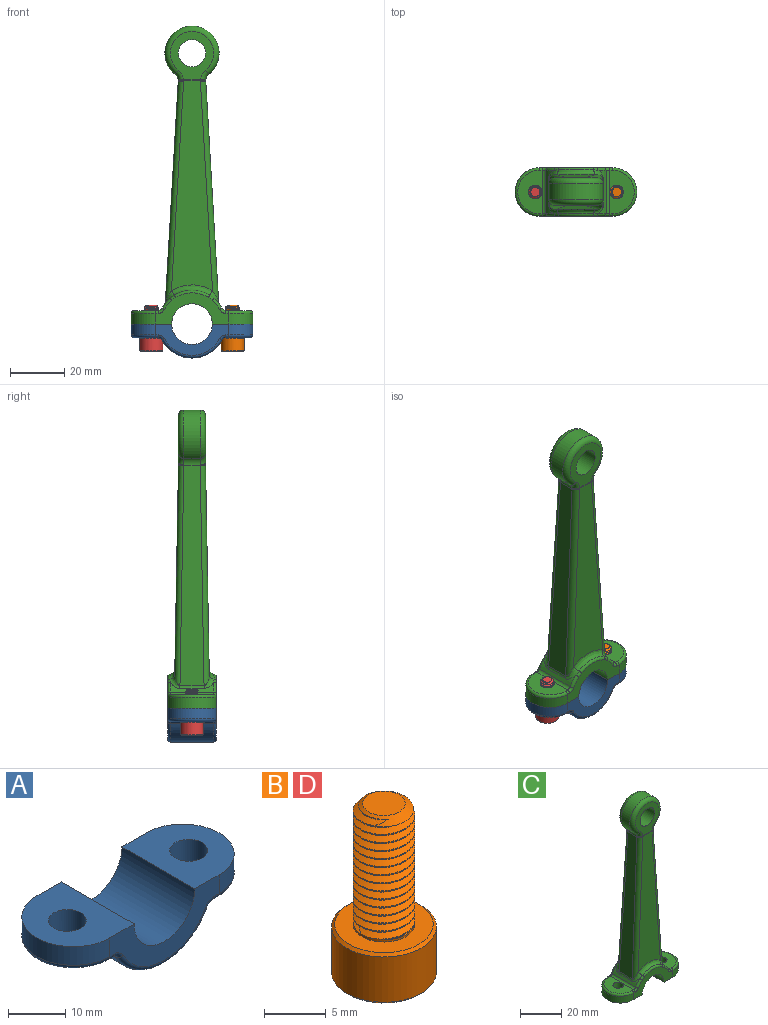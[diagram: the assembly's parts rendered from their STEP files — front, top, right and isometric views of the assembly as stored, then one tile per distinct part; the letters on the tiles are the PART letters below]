
ASSEMBLY  parts=4 mates=3
PART A: 30 faces, bbox 46.5x19.5x13.5 mm
  f0: cylinder r=12.5mm len=22.14mm, axis (0,1,0), area 404.5mm2, adj f12,f13,f14,f15,f16,f17,f23,f24
  f1: plane 18x15mm, normal (0,0,1), area 201mm2, adj f2,f6,f7,f9,f10
  f2: cylinder r=7.5mm len=18mm, axis (0,1,0), area 424.1mm2, adj f1,f3,f6,f7
  f3: plane 18x15mm, normal (0,0,1), area 201mm2, adj f2,f6,f7,f8,f11
  f4: plane 16x12mm, normal (0,0,-1), area 103.9mm2, adj f11,f12,f14,f17,f27,f28,f29
  f5: plane 16x12mm, normal (0,0,-1), area 103.9mm2, adj f10,f13,f15,f16,f18,f19,f20
  f6: plane 27x11.5mm, normal (0,-1,0), area 138.1mm2, adj f1,f2,f3,f8,f9,f19,f21,f23
  f7: plane 27x11.5mm, normal (0,1,0), area 138.1mm2, adj f1,f2,f3,f8,f9,f20,f22,f24
  f8: cylinder r=9mm len=18mm, axis (0,0,1), area 113.1mm2, adj f3,f6,f7,f29
  f9: cylinder r=9mm len=18mm, axis (0,0,-1), area 113.1mm2, adj f1,f6,f7,f18
  f10: cylinder r=3.3mm len=6.6mm, axis (0,0,1), area 103.7mm2, adj f1,f5
  f11: cylinder r=3.3mm len=6.6mm, axis (0,0,1), area 103.7mm2, adj f3,f4
  f12: cylinder r=5.5mm len=9.69mm, axis (0,0,1), area 21.4mm2, adj f0,f4,f14,f17
  f13: cylinder r=5.5mm len=9.69mm, axis (0,0,1), area 21.4mm2, adj f0,f5,f15,f16
  f14: cylinder r=1.5mm len=4.15mm, axis (0,1,0), area 6mm2, adj f0,f4,f12,f26
  f15: cylinder r=1.5mm len=4.15mm, axis (0,1,0), area 6mm2, adj f0,f5,f13,f22
  f16: cylinder r=1.5mm len=4.15mm, axis (0,1,0), area 6mm2, adj f0,f5,f13,f21
  f17: cylinder r=1.5mm len=4.15mm, axis (0,1,0), area 6mm2, adj f0,f4,f12,f25
  f18: torus R=8mm, axis (0,0,-1), area 42.6mm2, adj f5,f9,f19,f20
  f19: cylinder r=1mm len=1.1mm, axis (-1,0,0), area 1.7mm2, adj f5,f6,f18,f21
  f20: cylinder r=1mm len=1.1mm, axis (1,0,0), area 1.7mm2, adj f5,f7,f18,f22
  f21: torus R=2.5mm, axis (0,-1,0), area 3.2mm2, adj f6,f16,f19,f23
  f22: torus R=2.5mm, axis (0,-1,0), area 3.2mm2, adj f7,f15,f20,f24
  f23: torus R=11.5mm, axis (0,-1,0), area 41.5mm2, adj f0,f6,f21,f25
  f24: torus R=11.5mm, axis (0,-1,0), area 41.5mm2, adj f0,f7,f22,f26
  f25: torus R=2.5mm, axis (0,-1,0), area 3.2mm2, adj f6,f17,f23,f27
  f26: torus R=2.5mm, axis (0,-1,0), area 3.2mm2, adj f7,f14,f24,f28
  f27: cylinder r=1mm len=1.1mm, axis (-1,0,0), area 1.7mm2, adj f4,f6,f25,f29
  f28: cylinder r=1mm len=1.1mm, axis (1,0,0), area 1.7mm2, adj f4,f7,f26,f29
  f29: torus R=8mm, axis (0,0,-1), area 42.6mm2, adj f4,f8,f27,f28
PART B: 39 faces, bbox 9.4x9.4x18 mm
  f0: cone r=2.5mm half-angle=67.5deg, axis (0,0,-1), area 4.1mm2, adj f1,f18,f19,f38
  f1: cylinder r=1.98mm len=11.41mm, axis (0,0,-1), area 17.7mm2, adj f0,f2,f18,f38
  f2: cone r=1.73mm half-angle=55deg, axis (0,0,-1), area 7.9mm2, adj f1,f3,f4,f18,f38
  f3: plane 3.45x3.45mm, normal (0,0,1), area 9.4mm2, adj f2
  f4: cylinder r=2.5mm len=5mm, axis (0,0,1), area 1mm2, adj f2,f5,f18,f38
  f5: cylinder r=2.5mm len=5mm, axis (0,0,1), area 1.6mm2, adj f4,f6,f18,f38
  f6: cylinder r=2.5mm len=5mm, axis (0,0,1), area 1.6mm2, adj f5,f7,f18,f38
  f7: cylinder r=2.5mm len=5mm, axis (0,0,1), area 1.6mm2, adj f6,f8,f18,f38
  f8: cylinder r=2.5mm len=5mm, axis (0,0,1), area 1.6mm2, adj f7,f9,f18,f38
  f9: cylinder r=2.5mm len=5mm, axis (0,0,1), area 1.6mm2, adj f8,f10,f18,f38
  f10: cylinder r=2.5mm len=5mm, axis (0,0,1), area 1.6mm2, adj f9,f11,f18,f38
  f11: cylinder r=2.5mm len=5mm, axis (0,0,1), area 1.6mm2, adj f10,f12,f18,f38
  f12: cylinder r=2.5mm len=5mm, axis (0,0,1), area 1.6mm2, adj f11,f13,f18,f38
  f13: cylinder r=2.5mm len=5mm, axis (0,0,1), area 1.6mm2, adj f12,f14,f18,f38
  f14: cylinder r=2.5mm len=5mm, axis (0,0,1), area 1.6mm2, adj f13,f15,f18,f38
  f15: cylinder r=2.5mm len=5mm, axis (0,0,1), area 1.6mm2, adj f14,f16,f18,f38
  f16: cylinder r=2.5mm len=5mm, axis (0,0,1), area 1.6mm2, adj f15,f17,f18,f38
  f17: cylinder r=2.5mm len=5mm, axis (0,0,1), area 1.6mm2, adj f16,f18,f19,f38
  f18: bspline ~11.71x5mm, area 119.7mm2, adj f0,f1,f2,f4,f5,f6,f7,f8
  f19: cylinder r=2.5mm len=5mm, axis (0,0,1), area 3.8mm2, adj f0,f17,f18,f20,f38
  f20: plane 7.99x7.99mm, normal (0,0,1), area 30.5mm2, adj f19,f21
  f21: cone r=4.25mm half-angle=45deg, axis (0,0,-1), area 9.3mm2, adj f20,f22
  f22: cylinder r=4.25mm len=8.5mm, axis (0,0,1), area 119.9mm2, adj f21,f23
  f23: cone r=4mm half-angle=45deg, axis (0,0,1), area 9.3mm2, adj f22,f24
  f24: plane 8.74x8.74mm, normal (0,0,-1), area 33.4mm2, adj f23,f25,f33,f34,f35,f36,f37
  f25: cone r=2.31mm half-angle=45deg, axis (0,0,-1), area 0mm2, adj f24,f26
  f26: plane 3.88x2.88mm, normal (-0.5,-0.87,0), area 6.5mm2, adj f25,f27,f31,f32
  f27: plane 4.62x4mm, normal (0,0,-1), area 13.9mm2, adj f26,f28,f29,f30,f31,f32
  f28: plane 3.22x2.53mm, normal (1,0,0), area 6.5mm2, adj f27,f29,f32,f36
  f29: plane 3.88x2.88mm, normal (0.5,0.87,0), area 6.5mm2, adj f27,f28,f30,f35
  f30: plane 3.88x2.88mm, normal (-0.5,0.87,0), area 6.5mm2, adj f27,f29,f31,f34
  f31: plane 3.88x3.18mm, normal (-1,0,0), area 6.5mm2, adj f26,f27,f30,f33
  f32: plane 3.88x2.88mm, normal (0.5,-0.87,0), area 6.5mm2, adj f26,f27,f28,f37
  f33: cone r=2.31mm half-angle=45deg, axis (0,0,-1), area 0mm2, adj f24,f31
  f34: cone r=2.31mm half-angle=45deg, axis (0,0,-1), area 0mm2, adj f24,f30
  f35: cone r=2.31mm half-angle=45deg, axis (0,0,-1), area 0mm2, adj f24,f29
  f36: cone r=2.31mm half-angle=45deg, axis (0,0,-1), area 0.5mm2, adj f24,f28
  f37: cone r=2.31mm half-angle=45deg, axis (0,0,-1), area 0mm2, adj f24,f32
  f38: bspline ~12.22x5mm, area 119.8mm2, adj f0,f1,f2,f4,f5,f6,f7,f8
PART C: 73 faces, bbox 46.5x19.5x110.8 mm
  f0: cylinder r=12.5mm len=16mm, axis (0,1,0), area 38.3mm2, adj f45,f47,f49,f52,f53,f65
  f1: plane 81.35x8.89mm, normal (-1,0,0.06), area 607.2mm2, adj f23,f33,f42,f47
  f2: plane 81.35x8.89mm, normal (1,0,0.06), area 607.2mm2, adj f24,f25,f34,f46
  f3: cylinder r=10mm len=20mm, axis (0,1,0), area 296.4mm2, adj f23,f24,f29,f38
  f4: plane 17.82x16mm, normal (0,1,0), area 137.2mm2, adj f8,f22,f37,f38,f39
  f5: plane 77.49x15.15mm, normal (0,1,0.02), area 804.4mm2, adj f22,f34,f35,f41,f42,f43
  f6: plane 17.82x16mm, normal (0,-1,0), area 137.2mm2, adj f8,f21,f28,f29,f30
  f7: plane 77.49x15.15mm, normal (0,-1,0.02), area 804.4mm2, adj f21,f25,f26,f32,f33,f50
  f8: cylinder r=5mm len=10mm, axis (0,1,0), area 314.2mm2, adj f4,f6
  f9: cylinder r=12.5mm len=16mm, axis (0,1,0), area 38.3mm2, adj f44,f46,f48,f51,f60,f72
  f10: plane 18x15mm, normal (0,0,-1), area 215.6mm2, adj f13,f15,f16,f18,f20
  f11: plane 18x15mm, normal (0,0,-1), area 215.6mm2, adj f13,f15,f16,f17,f19
  f12: plane 16x9.1mm, normal (0,0,1), area 98.5mm2, adj f20,f51,f64,f66,f68
  f13: cylinder r=7.5mm len=18mm, axis (0,1,0), area 424.1mm2, adj f10,f11,f15,f16
  f14: plane 16x9.1mm, normal (0,0,1), area 98.5mm2, adj f19,f52,f57,f59,f61
  f15: plane 27x11.52mm, normal (0,1,0), area 138.4mm2, adj f10,f11,f13,f17,f18,f53,f54,f55
  f16: plane 27x11.52mm, normal (0,-1,0), area 138.4mm2, adj f10,f11,f13,f17,f18,f61,f63,f65
  f17: cylinder r=9mm len=18mm, axis (0,0,1), area 113.1mm2, adj f11,f15,f16,f59
  f18: cylinder r=9mm len=18mm, axis (0,0,-1), area 113.1mm2, adj f10,f15,f16,f66
  f19: cylinder r=2.5mm len=5mm, axis (0,0,1), area 78.5mm2, adj f11,f14
  f20: cylinder r=2.5mm len=5mm, axis (0,0,1), area 78.5mm2, adj f10,f12
  f21: cylinder r=20mm len=6.21mm, axis (1,0,0), area 2.2mm2, adj f6,f7,f27,f31
  f22: cylinder r=20mm len=6.21mm, axis (1,0,0), area 2.2mm2, adj f4,f5,f36,f40
  f23: cylinder r=3mm len=6.02mm, axis (0,1,0), area 17.2mm2, adj f1,f3,f30,f31,f32,f39,f40,f41
  f24: cylinder r=3mm len=6.02mm, axis (0,1,0), area 17.2mm2, adj f2,f3,f26,f27,f28,f35,f36,f37
  f25: cylinder r=2mm len=81.43mm, axis (0.06,-0.02,-1), area 249.4mm2, adj f2,f7,f26,f48
  f26: bspline ~2.01x2mm, area 0.6mm2, adj f7,f24,f25,f27
  f27: bspline ~2.08x2.03mm, area 0.8mm2, adj f21,f24,f26,f28
  f28: torus R=5mm, axis (0,1,0), area 9.7mm2, adj f6,f24,f27,f29
  f29: torus R=8mm, axis (0,1,0), area 143.9mm2, adj f3,f6,f28,f30
  f30: torus R=5mm, axis (0,1,0), area 9.7mm2, adj f6,f23,f29,f31
  f31: bspline ~2.08x2.03mm, area 0.8mm2, adj f21,f23,f30,f32
  f32: bspline ~2.01x2mm, area 0.6mm2, adj f7,f23,f31,f33
  f33: cylinder r=2mm len=81.43mm, axis (0.06,0.02,1), area 249.4mm2, adj f1,f7,f32,f49
  f34: cylinder r=2mm len=81.43mm, axis (-0.06,-0.02,1), area 249.4mm2, adj f2,f5,f35,f44
  f35: bspline ~2.01x2mm, area 0.6mm2, adj f5,f24,f34,f36
  f36: bspline ~2.08x2.01mm, area 0.8mm2, adj f22,f24,f35,f37
  f37: torus R=5mm, axis (0,1,0), area 9.7mm2, adj f4,f24,f36,f38
  f38: torus R=8mm, axis (0,1,0), area 143.9mm2, adj f3,f4,f37,f39
  f39: torus R=5mm, axis (0,1,0), area 9.7mm2, adj f4,f23,f38,f40
  f40: bspline ~2.08x2.01mm, area 0.8mm2, adj f22,f23,f39,f41
  f41: bspline ~2.01x2mm, area 0.6mm2, adj f5,f23,f40,f42
  f42: cylinder r=2mm len=81.43mm, axis (-0.06,0.02,-1), area 249.4mm2, adj f1,f5,f41,f45
  f43: bspline ~15.15x3.79mm, area 41.8mm2, adj f5,f44,f45,f56
  f44: bspline ~5.22x4.45mm, area 11.6mm2, adj f9,f34,f43,f46,f58
  f45: bspline ~5.64x4.47mm, area 11.6mm2, adj f0,f42,f43,f47,f54
  f46: cylinder r=2mm len=8.89mm, axis (0,1,0), area 10mm2, adj f2,f9,f44,f48
  f47: cylinder r=2mm len=8.89mm, axis (0,1,0), area 10mm2, adj f0,f1,f45,f49
  f48: bspline ~5.64x4.47mm, area 11.6mm2, adj f9,f25,f46,f50,f71
  f49: bspline ~5.64x4.47mm, area 11.6mm2, adj f0,f33,f47,f50,f67
  f50: bspline ~15.15x3.79mm, area 41.8mm2, adj f7,f48,f49,f69
  f51: cylinder r=1.5mm len=16mm, axis (0,1,0), area 26.1mm2, adj f9,f12,f62,f70
  f52: cylinder r=1.5mm len=16mm, axis (0,1,0), area 26.1mm2, adj f0,f14,f55,f63
  f53: torus R=11.5mm, axis (0,-1,0), area 7.3mm2, adj f0,f15,f54,f55
  f54: bspline ~3.95x3.3mm, area 2.8mm2, adj f15,f45,f53,f56
  f55: torus R=2.5mm, axis (0,-1,0), area 3.2mm2, adj f15,f52,f53,f57
  f56: bspline ~15.4x3.43mm, area 19.4mm2, adj f15,f43,f54,f58
  f57: cylinder r=1mm len=1.1mm, axis (-1,0,0), area 1.7mm2, adj f14,f15,f55,f59
  f58: bspline ~2.83x2.44mm, area 2.8mm2, adj f15,f44,f56,f60
  f59: torus R=8mm, axis (0,0,1), area 42.6mm2, adj f14,f17,f57,f61
  f60: torus R=11.5mm, axis (0,-1,0), area 7.3mm2, adj f9,f15,f58,f62
  f61: cylinder r=1mm len=1.1mm, axis (1,0,0), area 1.7mm2, adj f14,f16,f59,f63
  f62: torus R=2.5mm, axis (0,-1,0), area 3.2mm2, adj f15,f51,f60,f64
  f63: torus R=2.5mm, axis (0,-1,0), area 3.2mm2, adj f16,f52,f61,f65
  f64: cylinder r=1mm len=1.1mm, axis (-1,0,0), area 1.7mm2, adj f12,f15,f62,f66
  f65: torus R=11.5mm, axis (0,-1,0), area 7.3mm2, adj f0,f16,f63,f67
  f66: torus R=8mm, axis (0,0,1), area 42.6mm2, adj f12,f18,f64,f68
  f67: bspline ~3.24x2.75mm, area 2.8mm2, adj f16,f49,f65,f69
  f68: cylinder r=1mm len=1.1mm, axis (1,0,0), area 1.7mm2, adj f12,f16,f66,f70
  f69: bspline ~15.4x3.43mm, area 19.4mm2, adj f16,f50,f67,f71
  f70: torus R=2.5mm, axis (0,-1,0), area 3.2mm2, adj f16,f51,f68,f72
  f71: bspline ~3.01x2.6mm, area 2.8mm2, adj f16,f48,f69,f72
  f72: torus R=11.5mm, axis (0,-1,0), area 7.3mm2, adj f9,f16,f70,f71
PART D: same geometry as B
PLACE A at identity
PLACE B t=(15,0,7)mm
PLACE C at identity fixed
PLACE D t=(-15,0,7)mm
MATE revolute D.f1 <-> A.f12  axis (0,0,1) through (-15,0,-5)mm
MATE revolute B.f1 <-> A.f13  axis (0,0,1) through (15,0,-5)mm
MATE fastened A.f9 <-> C.f66  axis (0,0,1) through (13.5,0,0)mm
